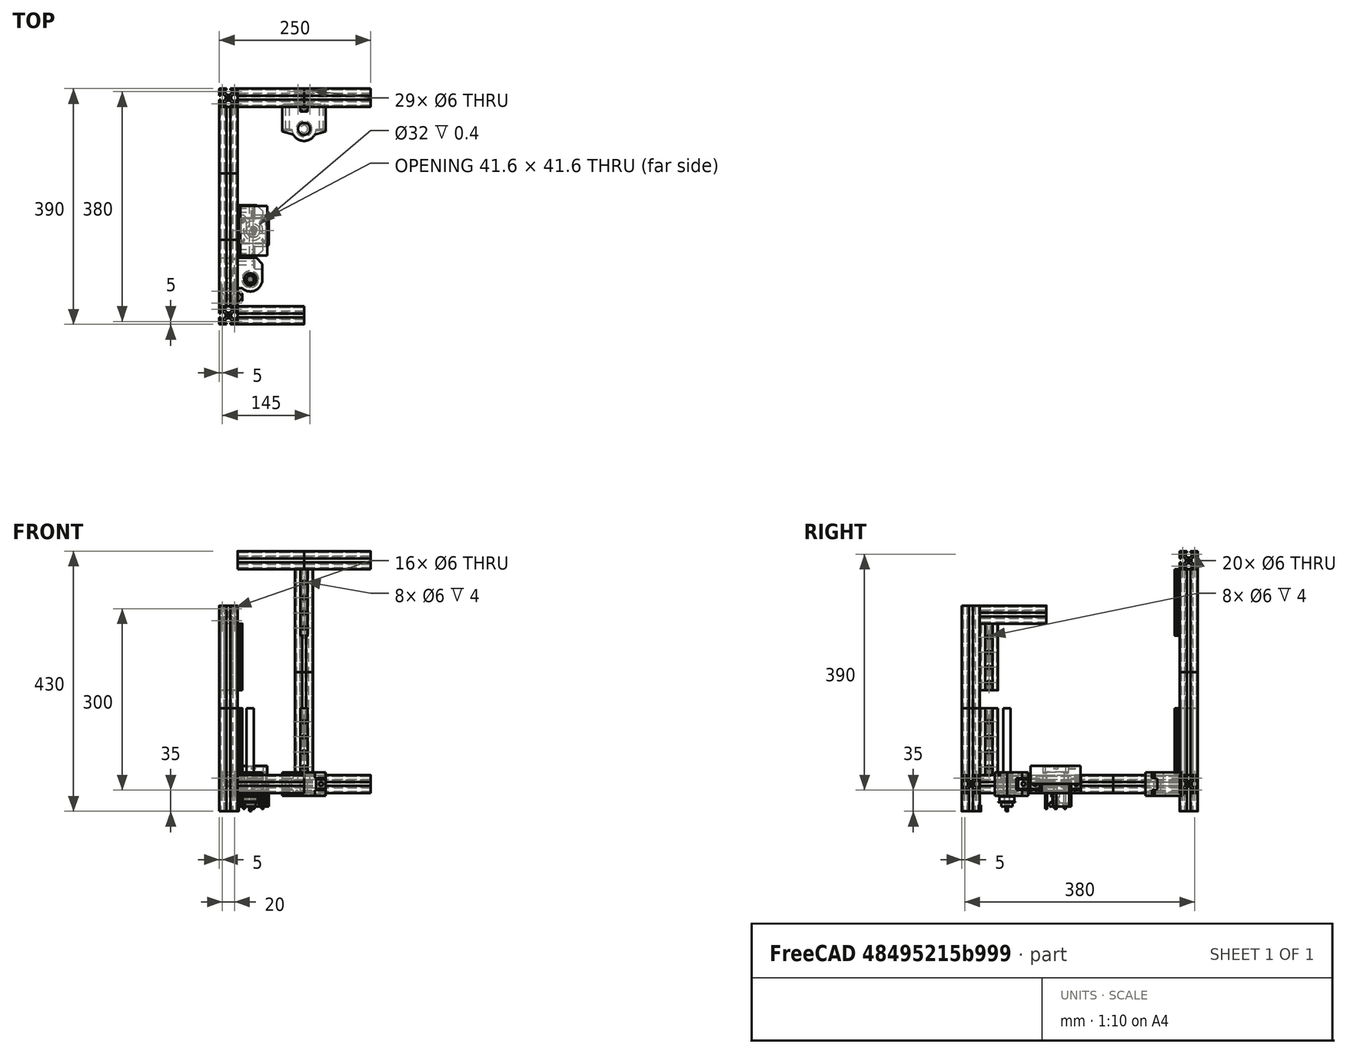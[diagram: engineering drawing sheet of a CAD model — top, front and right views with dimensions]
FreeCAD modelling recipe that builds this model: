
FCSTD DOCUMENT  (FreeCAD 0.18R16146 (Git))
Label: z-belt
License: All rights reserved
LicenseURL: http://en.wikipedia.org/wiki/All_rights_reserved
objects: Part::Cylinder×31, Part::Box×30, Part::Feature×29, Part::Chamfer×21, Part::MultiFuse×16, Part::Cut×15, App::DocumentObjectGroup×1, Part::Fillet×1
note: 143 computed .brp shape members not serialized (recipe doc carries the construction recipe); baked Part::Feature solids carry a one-line shape summary decoded from their .brp

FEATURE [Part::Feature] Fusion002  label="extrusion-3030-002"
  Placement = pos=(-7e-15,0,30) rot=(0,1,0;1.5708rad)
  shape: bbox 110 x 30 x 30 mm, 63 faces (baked)
FEATURE [Part::Feature] Fusion003  label="extrusion-3030-003"
  Placement = pos=(-30,-7e-15,30) rot=(0.57735,-0.57735,-0.57735;4.18879rad)
  shape: bbox 30 x 110 x 30 mm, 63 faces (baked)
FEATURE [Part::Feature] Fusion004  label="extrusion-3030-004"
  Placement = pos=(0,30,60) rot=(0,0,1;0rad)
  shape: bbox 30 x 30 x 110 mm, 63 faces (baked)
FEATURE [Part::Feature] Fusion006  label="extrusion-3030-001"
  shape: bbox 30 x 30 x 170 mm, 63 faces (baked)
FEATURE [Part::Feature] Common001  label="MGN12-rail"
  Placement = pos=(4,15,60) rot=(0.707107,0,0.707107;3.14159rad)
  shape: bbox 8 x 12 x 110 mm, 48 faces (baked)
FEATURE [Part::Feature] Chamfer001  label="SFU1204"
  Placement = pos=(21.15,44.62,10) rot=(0,0,1;0rad)
  shape: bbox 12 x 12 x 160 mm, 10 faces (baked)
FEATURE [Part::Feature] Cut001  label="pulley-40t"
  Placement = pos=(21.15,44.62,25) rot=(0,1,0;3.14159rad)
  shape: bbox 28 x 28 x 17 mm, 10 faces (baked)
FEATURE [Part::Cylinder] Cylinder  label="pos-4462-2115"
  Angle = 360
  AttacherType = Attacher::AttachEngine3D
  Height = 10
  Placement = pos=(21.15,44.52,0) rot=(0,0,1;0rad)
  Radius = 2
FEATURE [Part::Cylinder] Cylinder001  label="pos-3659"
  Angle = 360
  AttacherType = Attacher::AttachEngine3D
  Height = 10
  Radius = 2
FEATURE [Part::Box] Box  label="Cube"
  AttacherType = Attacher::AttachEngine3D
  Height = 4
  Length = 71.15
  Placement = pos=(-30,30,60) rot=(0,0,1;0rad)
  Width = 50
FEATURE [Part::Feature] Cut002001  label="collar"
  Placement = pos=(21.15,44.62,55) rot=(0,0,1;0rad)
  shape: bbox 18 x 18 x 8 mm, 7 faces (baked)
FEATURE [Part::Feature] Cut002002  label="thrust-bearing"
  Placement = pos=(21.15,44.62,49.5) rot=(0,0,1;0rad)
  shape: bbox 18 x 18 x 5.5 mm, 12 faces (baked)
FEATURE [Part::Feature] Chamfer002  label="6000zz"
  Placement = pos=(21.15,44.62,25.5) rot=(0,0,1;0rad)
  shape: bbox 26 x 26 x 8 mm, 8 faces (baked)
FEATURE [Part::Cylinder] Cylinder002  label="screw-cut"
  Angle = 360
  AttacherType = Attacher::AttachEngine3D
  Height = 15
  Placement = pos=(21.15,44.52,34.5) rot=(0,0,1;0rad)
  Radius = 6
FEATURE [Part::Cylinder] Cylinder003  label="top-bearing-cut"
  Angle = 360
  AttacherType = Attacher::AttachEngine3D
  Height = 15
  Placement = pos=(21.15,44.52,49.5) rot=(0,0,1;0rad)
  Radius = 10
FEATURE [Part::Cylinder] Cylinder004  label="btm-bearing-cut"
  Angle = 360
  AttacherType = Attacher::AttachEngine3D
  Height = 9
  Placement = pos=(21.15,44.52,25.5) rot=(0,0,1;0rad)
  Radius = 13.1
FEATURE [Part::Cylinder] Cylinder005  label="round-body"
  Angle = 360
  AttacherType = Attacher::AttachEngine3D
  Height = 38.5
  Placement = pos=(21.15,44.52,25.5) rot=(0,0,1;0rad)
  Radius = 20
FEATURE [Part::Box] Box003  label="Cube003"
  AttacherType = Attacher::AttachEngine3D
  Height = 6
  Length = 2
  Placement = pos=(-2,30,42) rot=(0,0,1;0rad)
  Width = 34.52
FEATURE [Part::Feature] Fusion007  label="extrusion-3030-005"
  Placement = pos=(-30,110,30) rot=(0.57735,-0.57735,-0.57735;4.18879rad)
  shape: bbox 30 x 110 x 30 mm, 63 faces (baked)
FEATURE [Part::Box] Box004  label="Cube004"
  AttacherType = Attacher::AttachEngine3D
  Height = 34.5
  Length = 41.15
  Placement = pos=(0,30.02,25.5) rot=(0,0,1;0rad)
  Width = 49.98
FEATURE [Part::Box] Box005  label="Cube005"
  AttacherType = Attacher::AttachEngine3D
  Height = 20
  Length = 41.15
  Placement = pos=(27,61.52,35) rot=(0,0,1;0rad)
  Width = 35.48
FEATURE [Part::MultiFuse] Fusion008
  Shapes = -> [Cylinder004,Cylinder003,Cylinder002]
FEATURE [Part::Cylinder] Cylinder006  label="Cylinder"
  Angle = 360
  AttacherType = Attacher::AttachEngine3D
  Height = 10
  Placement = pos=(-15,42.5,60) rot=(0,0,1;0rad)
  Radius = 3.2
FEATURE [Part::Cylinder] Cylinder007  label="Cylinder001"
  Angle = 360
  AttacherType = Attacher::AttachEngine3D
  Height = 33
  Placement = pos=(0,72,45) rot=(0,1,0;1.5708rad)
  Radius = 3.2
FEATURE [Part::Cylinder] Cylinder008  label="Cylinder002"
  Angle = 360
  AttacherType = Attacher::AttachEngine3D
  Height = 10
  Placement = pos=(-15,67.5,60) rot=(0,0,1;0rad)
  Radius = 3.2
FEATURE [Part::Feature] Cut002003006  label="Pulley-16T"
  Placement = pos=(26,125,15.3) rot=(0,0,1;3.14159rad)
  shape: bbox 13.9 x 13.9 x 15.5 mm, 10 faces (baked)
FEATURE [Part::Cylinder] Cylinder010  label="motor-center"
  Angle = 360
  AttacherType = Attacher::AttachEngine3D
  Height = 10
  Placement = pos=(26,125,4) rot=(0,0,1;0rad)
  Radius = 2
FEATURE [Part::Feature] Fusion001  label="nema17-39mm"
  Placement = pos=(26,125,10) rot=(0,0,1;0rad)
  shape: bbox 42 x 54 x 63 mm, 80 faces (baked)
FEATURE [Part::Feature] Chamfer014  label="MR115ZZ"
  Placement = pos=(26,125,10) rot=(0,0,1;0rad)
  shape: bbox 11 x 11 x 4 mm, 8 faces (baked)
FEATURE [Part::Box] Box006  label="Cube006"
  AttacherType = Attacher::AttachEngine3D
  Height = 30
  Length = 4.85
  Placement = pos=(0,83,30) rot=(0,0,1;0rad)
  Width = 84
FEATURE [Part::Box] Box008  label="Cube008"
  AttacherType = Attacher::AttachEngine3D
  Height = 30
  Length = 48
  Placement = pos=(0,99,30) rot=(0,0,1;0rad)
  Width = 4.85
FEATURE [Part::Box] Box009  label="Cube009"
  AttacherType = Attacher::AttachEngine3D
  Height = 30
  Length = 48
  Placement = pos=(0,146.15,30) rot=(0,0,1;0rad)
  Width = 4.85
FEATURE [Part::Box] Box010  label="Cube010"
  AttacherType = Attacher::AttachEngine3D
  Height = 15
  Length = 4.85
  Placement = pos=(47.15,99,30) rot=(0,0,1;0rad)
  Width = 52
FEATURE [Part::Cylinder] Cylinder011  label="center-slot"
  Angle = 360
  AttacherType = Attacher::AttachEngine3D
  Height = 23
  Placement = pos=(26,125,23) rot=(0,0,1;0rad)
  Radius = 11.05
FEATURE [Part::Box] Box011  label="Cube011"
  AttacherType = Attacher::AttachEngine3D
  Height = 4
  Length = 52
  Placement = pos=(0,99,30) rot=(0,0,1;0rad)
  Width = 52
FEATURE [Part::Cylinder] Cylinder012  label="motor-bolt-4"
  Angle = 360
  AttacherType = Attacher::AttachEngine3D
  Height = 47
  Placement = pos=(41.5,140.5,4) rot=(0,0,1;0rad)
  Radius = 1.6
FEATURE [Part::Cylinder] Cylinder013  label="motor-bolt-3"
  Angle = 360
  AttacherType = Attacher::AttachEngine3D
  Height = 47
  Placement = pos=(10.5,140.5,4) rot=(0,0,1;0rad)
  Radius = 1.6
FEATURE [Part::Cylinder] Cylinder014  label="motor-bolt-2"
  Angle = 360
  AttacherType = Attacher::AttachEngine3D
  Height = 47
  Placement = pos=(10.5,109.5,4) rot=(0,0,1;0rad)
  Radius = 1.6
FEATURE [Part::Cylinder] Cylinder015  label="motor-bolt-1"
  Angle = 360
  AttacherType = Attacher::AttachEngine3D
  Height = 47
  Placement = pos=(41.5,109.5,4) rot=(0,0,1;0rad)
  Radius = 1.6
FEATURE [Part::Cylinder] Cylinder016  label="motor-bolt-005"
  Angle = 360
  AttacherType = Attacher::AttachEngine3D
  Height = 47
  Placement = pos=(41.5,140.5,4) rot=(0,0,1;0rad)
  Radius = 1.6
FEATURE [Part::Cylinder] Cylinder017  label="motor-bolt-006"
  Angle = 360
  AttacherType = Attacher::AttachEngine3D
  Height = 47
  Placement = pos=(41.5,109.5,4) rot=(0,0,1;0rad)
  Radius = 1.6
FEATURE [Part::Cylinder] Cylinder018  label="motor-bolt-007"
  Angle = 360
  AttacherType = Attacher::AttachEngine3D
  Height = 47
  Placement = pos=(10.5,109.5,4) rot=(0,0,1;0rad)
  Radius = 1.6
FEATURE [Part::Cylinder] Cylinder019  label="motor-bolt-008"
  Angle = 360
  AttacherType = Attacher::AttachEngine3D
  Height = 47
  Placement = pos=(10.5,140.5,4) rot=(0,0,1;0rad)
  Radius = 1.6
FEATURE [Part::MultiFuse] Fusion011
  Shapes = -> [Cylinder015,Cylinder014,Cylinder013,Cylinder012]
FEATURE [Part::Cut] Cut002003007
  Base = -> Box011
  Tool = -> Fusion011
FEATURE [Part::Box] Box012  label="Cube012"
  AttacherType = Attacher::AttachEngine3D
  Height = 30
  Length = 44
  Placement = pos=(5,84,63) rot=(0,0,1;0rad)
  Width = 82
FEATURE [Part::Chamfer] Chamfer018
  Base = -> Box012
  Edges = 1 edges r=15: [Edge4]
  Placement = pos=(0,0,-18) rot=(0,0,1;0rad)
FEATURE [Part::Cylinder] Cylinder020  label="Cylinder004"
  Angle = 360
  AttacherType = Attacher::AttachEngine3D
  Height = 46
  Placement = pos=(0,91,45) rot=(0,1,0;1.5708rad)
  Radius = 3.2
FEATURE [Part::Cylinder] Cylinder021  label="Cylinder005"
  Angle = 360
  AttacherType = Attacher::AttachEngine3D
  Height = 46
  Placement = pos=(0,159,45) rot=(0,1,0;1.5708rad)
  Radius = 3.2
FEATURE [Part::Cut] Cut002003010
  Base = -> Cut002003007
  Tool = -> Cylinder011
FEATURE [Part::Box] Box013  label="Cube013"
  AttacherType = Attacher::AttachEngine3D
  Height = 22
  Length = 52
  Placement = pos=(0,121,8) rot=(0,0,1;0rad)
  Width = 30
FEATURE [Part::Cylinder] Cylinder024  label="shhaft-cut"
  Angle = 360
  AttacherType = Attacher::AttachEngine3D
  Height = 10
  Placement = pos=(26,125,7) rot=(0,0,1;0rad)
  Radius = 3
FEATURE [Part::Cylinder] Cylinder025  label="shaft-br-cut"
  Angle = 360
  AttacherType = Attacher::AttachEngine3D
  Height = 4
  Placement = pos=(26,125,10) rot=(0,0,1;0rad)
  Radius = 5.6
FEATURE [Part::Box] Box014  label="Cube014"
  AttacherType = Attacher::AttachEngine3D
  Height = 16
  Length = 32
  Placement = pos=(10,96,14) rot=(0,0,1;0rad)
  Width = 30
FEATURE [Part::Cylinder] Cylinder027  label="Cylinder008"
  Angle = 360
  AttacherType = Attacher::AttachEngine3D
  Height = 6
  Placement = pos=(26,125,8) rot=(0,0,1;0rad)
  Radius = 10
FEATURE [Part::MultiFuse] Fusion018
  Shapes = -> [Box013,Cylinder027]
FEATURE [Part::Chamfer] Chamfer020
  Base = -> Box014
  Edges = 2 edges r=5: [Edge3,Edge7]
FEATURE [Part::Chamfer] Chamfer021
  Base = -> Fusion018
  Edges = 2 edges r=5: [Edge1,Edge10]
FEATURE [Part::Chamfer] Chamfer023
  Base = -> Chamfer021
  Edges = 2 edges r=3: [Edge3,Edge13]
FEATURE [Part::Cylinder] Cylinder030  label="motor-bolt-011"
  Angle = 360
  AttacherType = Attacher::AttachEngine3D
  Height = 47
  Placement = pos=(10.5,140.5,4) rot=(0,0,1;0rad)
  Radius = 1.65
FEATURE [Part::Cylinder] Cylinder031  label="motor-bolt-012"
  Angle = 360
  AttacherType = Attacher::AttachEngine3D
  Height = 47
  Placement = pos=(41.5,140.5,4) rot=(0,0,1;0rad)
  Radius = 1.65
FEATURE [Part::MultiFuse] Fusion020
  Shapes = -> [Cylinder017,Cylinder018,Cylinder019,Cylinder016]
FEATURE [Part::Cylinder] Cylinder032  label="motor-bolt-013"
  Angle = 360
  AttacherType = Attacher::AttachEngine3D
  Height = 5
  Placement = pos=(41.5,140.5,4) rot=(0,0,1;0rad)
  Radius = 3.5
FEATURE [Part::Cylinder] Cylinder033  label="motor-bolt-014"
  Angle = 360
  AttacherType = Attacher::AttachEngine3D
  Height = 5
  Placement = pos=(10.5,140.5,4) rot=(0,0,1;0rad)
  Radius = 3.5
FEATURE [Part::MultiFuse] Fusion021
  Shapes = -> [Cylinder030,Cylinder031]
FEATURE [Part::MultiFuse] Fusion022
  Placement = pos=(0,0,3) rot=(0,0,1;0rad)
  Shapes = -> [Cylinder032,Cylinder033]
FEATURE [Part::Box] Box015  label="Cube015"
  AttacherType = Attacher::AttachEngine3D
  Height = 22
  Length = 34
  Placement = pos=(9,145,8) rot=(0,0,1;0rad)
  Width = 10
FEATURE [Part::Chamfer] Chamfer024
  Base = -> Box015
  Edges = 2 edges r=7: [Edge1,Edge5]
FEATURE [Part::Box] Box016  label="Cube016"
  AttacherType = Attacher::AttachEngine3D
  Height = 16
  Length = 22
  Placement = pos=(15,121,14) rot=(0,0,1;0rad)
  Width = 30
FEATURE [Part::Feature] Fusion023  label="extrusion-3030-006"
  Placement = pos=(-30,220,30) rot=(0.57735,-0.57735,-0.57735;4.18879rad)
  shape: bbox 30 x 110 x 30 mm, 63 faces (baked)
FEATURE [Part::Feature] Fusion024  label="extrusion-3030-007"
  Placement = pos=(0,360,0) rot=(0,0,1;0rad)
  shape: bbox 30 x 30 x 170 mm, 63 faces (baked)
FEATURE [Part::Feature] Fusion025  label="extrusion-3030-008"
  Placement = pos=(-7e-15,360,30) rot=(0,1,0;1.5708rad)
  shape: bbox 110 x 30 x 30 mm, 63 faces (baked)
FEATURE [Part::Feature] Fusion026  label="extrusion-3030-009"
  Placement = pos=(110,360,30) rot=(0,1,0;1.5708rad)
  shape: bbox 110 x 30 x 30 mm, 63 faces (baked)
FEATURE [Part::Feature] Fusion027  label="extrusion-3030-010"
  Placement = pos=(125,360,60) rot=(0,0,1;0rad)
  shape: bbox 30 x 30 x 170 mm, 63 faces (baked)
FEATURE [Part::Feature] Fusion008001  label="bearing-cut-slot"
  Placement = pos=(88.85,248.79,0) rot=(0,0,1;0rad)
  shape: bbox 26.2 x 26.2 x 39 mm, 7 faces (baked)
FEATURE [Part::Feature] Common002  label="MGN12-rail001"
  Placement = pos=(110,326,60) rot=(0.57735,-0.57735,0.57735;2.0944rad)
  shape: bbox 12 x 8 x 110 mm, 48 faces (baked)
FEATURE [Part::Box] Box017  label="Cube017"
  AttacherType = Attacher::AttachEngine3D
  Height = 38.5
  Length = 72
  Placement = pos=(74,284,25.5) rot=(0,0,1;0rad)
  Width = 46
FEATURE [Part::Box] Box018  label="Cube018"
  AttacherType = Attacher::AttachEngine3D
  Height = 4
  Length = 72
  Placement = pos=(74,330,60) rot=(0,0,1;0rad)
  Width = 4
FEATURE [Part::Box] Box019  label="Cube019"
  AttacherType = Attacher::AttachEngine3D
  Height = 4
  Length = 72
  Placement = pos=(74,330,25.5) rot=(0,0,1;0rad)
  Width = 5
FEATURE [Part::Box] Box020  label="Cube020"
  AttacherType = Attacher::AttachEngine3D
  Height = 20
  Length = 72
  Placement = pos=(74,284,35) rot=(0,0,1;0rad)
  Width = 9
FEATURE [Part::Box] Box021  label="Cube021"
  AttacherType = Attacher::AttachEngine3D
  Height = 6
  Length = 46
  Placement = pos=(87,330,42) rot=(0,0,1;0rad)
  Width = 2
FEATURE [Part::Cylinder] Cylinder035  label="Cylinder010"
  Angle = 360
  AttacherType = Attacher::AttachEngine3D
  Height = 46
  Placement = pos=(82,330,45) rot=(1,0,0;1.5708rad)
  Radius = 3.2
FEATURE [Part::Cylinder] Cylinder036  label="Cylinder011"
  Angle = 360
  AttacherType = Attacher::AttachEngine3D
  Height = 46
  Placement = pos=(138,330,45) rot=(1,0,0;1.5708rad)
  Radius = 3.2
FEATURE [Part::Box] Box022  label="Cube022"
  AttacherType = Attacher::AttachEngine3D
  Height = 4
  Length = 30.4
  Placement = pos=(94.8,329.8,60) rot=(0,0,1;0rad)
  Width = 2.2
FEATURE [Part::Box] Box023  label="Cube023"
  AttacherType = Attacher::AttachEngine3D
  Height = 4
  Length = 12.4
  Placement = pos=(103.8,321.8,60) rot=(0,0,1;0rad)
  Width = 10
FEATURE [Part::MultiFuse] Fusion008004
  Shapes = -> [Box023,Box022]
FEATURE [Part::Feature] Fusion008008  label="extrusion-3030-011"
  Placement = pos=(0,0,170) rot=(0,0,1;0rad)
  shape: bbox 30 x 30 x 170 mm, 63 faces (baked)
FEATURE [Part::Feature] Fusion008009  label="extrusion-3030-012"
  Placement = pos=(0,30,200) rot=(0,0,1;0rad)
  shape: bbox 30 x 30 x 110 mm, 63 faces (baked)
FEATURE [Part::Feature] Fusion008010  label="extrusion-3030-013"
  Placement = pos=(-30,-7e-15,310) rot=(0.57735,-0.57735,-0.57735;4.18879rad)
  shape: bbox 30 x 110 x 30 mm, 63 faces (baked)
FEATURE [Part::Feature] Common003  label="MGN12-rail002"
  Placement = pos=(4,15,200) rot=(0.707107,0,0.707107;3.14159rad)
  shape: bbox 8 x 12 x 110 mm, 48 faces (baked)
FEATURE [Part::Feature] Fusion008011  label="extrusion-3030-014"
  Placement = pos=(125,360,230) rot=(0,0,1;0rad)
  shape: bbox 30 x 30 x 170 mm, 63 faces (baked)
FEATURE [Part::Feature] Fusion008012  label="extrusion-3030-015"
  Placement = pos=(110,360,400) rot=(0,1,0;1.5708rad)
  shape: bbox 110 x 30 x 30 mm, 63 faces (baked)
FEATURE [Part::Feature] Fusion008013  label="extrusion-3030-016"
  Placement = pos=(-8.5e-14,360,400) rot=(0,1,0;1.5708rad)
  shape: bbox 110 x 30 x 30 mm, 63 faces (baked)
FEATURE [Part::Feature] Common004  label="MGN12-rail003"
  Placement = pos=(110,326,290) rot=(0.57735,-0.57735,0.57735;2.0944rad)
  shape: bbox 12 x 8 x 110 mm, 48 faces (baked)
FEATURE [App::DocumentObjectGroup] Group  label="Preference"
  Group = -> [Fusion002,Fusion003,Fusion004,Fusion006,Common001,Chamfer001,Cut001,Cylinder,Cylinder001,Cut002001,Cut002002,Chamfer002,Fusion007,Cut002003006,Cylinder010,Fusion001,Chamfer014,Fusion023,Fusion024,Fusion025,Fusion026,Fusion027,Common002,Fusion008008,Fusion008009,Fusion008010,Common003,Fusion008011,Fusion008012,Fusion008013,Common004]
FEATURE [Part::Box] Box024  label="Cube024"
  AttacherType = Attacher::AttachEngine3D
  Height = 4.5
  Length = 5
  Placement = pos=(-5,30.02,25.5) rot=(0,0,1;0rad)
  Width = 49.98
FEATURE [Part::Chamfer] Chamfer
  Base = -> Box
  Edges = 1 edges r=15: [Edge5]
FEATURE [Part::Chamfer] Chamfer033
  Base = -> Box004
  Edges = 1 edges r=15: [Edge5]
FEATURE [Part::MultiFuse] Fusion
  Shapes = -> [Box024,Chamfer033,Cylinder005,Chamfer,Box003]
FEATURE [Part::Cut] Cut
  Base = -> Fusion
  Tool = -> Box005
FEATURE [Part::Fillet] Fillet001
  Base = -> Cut
  Edges = 1 edges r=0.7: [Edge9]
FEATURE [Part::Chamfer] Chamfer034
  Base = -> Fillet001
  Edges = 3 edges r=10: [Edge45,Edge47,Edge71]
FEATURE [Part::Chamfer] Chamfer035
  Base = -> Chamfer034
  Edges = 1 edges r=1: [Edge26]
FEATURE [Part::Chamfer] Chamfer036
  Base = -> Chamfer035
  Edges = 2 edges r=3: [Edge69,Edge93]
FEATURE [Part::MultiFuse] Fusion008014
  Shapes = -> [Cylinder006,Cylinder008]
FEATURE [Part::Cut] Cut002003021002
  Base = -> Chamfer036
  Tool = -> Fusion008014
FEATURE [Part::Chamfer] Chamfer037
  Base = -> Cut002003021002
  Edges = 3 edges r=2: [Edge80,Edge85,Edge86]
FEATURE [Part::Cut] Cut002003021003
  Base = -> Chamfer037
  Tool = -> Cylinder007
FEATURE [Part::Cylinder] Cylinder034  label="Cylinder009"
  Angle = 360
  AttacherType = Attacher::AttachEngine3D
  Height = 38.5
  Placement = pos=(110,293.41,25.5) rot=(0,0,-1;1.5708rad)
  Radius = 20
FEATURE [Part::MultiFuse] Fusion008016
  Shapes = -> [Cylinder035,Cylinder036]
FEATURE [Part::MultiFuse] Fusion008017
  Shapes = -> [Box017,Box019,Box021,Box018]
FEATURE [Part::Cut] Cut002003021004
  Base = -> Fusion008017
  Tool = -> Box020
FEATURE [Part::Chamfer] Chamfer038
  Base = -> Cut002003021004
  Edges = 2 edges r=2: [Edge14,Edge17]
FEATURE [Part::Chamfer] Chamfer039
  Base = -> Chamfer038
  Edges = 2 edges: [Edge3 r1=5 r2=19,Edge10 r1=5 r2=19]
FEATURE [Part::Chamfer] Chamfer040
  Base = -> Chamfer039
  Edges = 1 edges: [Edge51 r1=5 r2=19]
FEATURE [Part::Chamfer] Chamfer041
  Base = -> Chamfer040
  Edges = 1 edges: [Edge22 r1=5 r2=19]
FEATURE [Part::MultiFuse] Fusion008018
  Shapes = -> [Chamfer041,Cylinder034]
FEATURE [Part::Cut] Cut002003021005
  Base = -> Fusion008018
  Tool = -> Fusion008016
FEATURE [Part::Cut] Cut002003021006
  Base = -> Cut002003021005
  Tool = -> Fusion008004
FEATURE [Part::MultiFuse] Fusion008019
  Shapes = -> [Fusion021,Fusion022]
FEATURE [Part::Cut] Cut002003021007
  Base = -> Chamfer023
  Tool = -> Chamfer020
FEATURE [Part::Cut] Cut002003021008
  Base = -> Cut002003021007
  Tool = -> Fusion008019
FEATURE [Part::Cut] Cut002003021009
  Base = -> Cut002003021008
  Tool = -> Chamfer024
FEATURE [Part::Cut] Cut002003021010
  Base = -> Cut002003021009
  Tool = -> Box016
FEATURE [Part::Cut] Cut002003021011
  Base = -> Cut002003021010
  Tool = -> Cylinder024
FEATURE [Part::Box] Box025  label="Cube025"
  AttacherType = Attacher::AttachEngine3D
  Height = 30
  Length = 27
  Placement = pos=(0,83,30) rot=(0,0,1;0rad)
  Width = 16
FEATURE [Part::Box] Box026  label="Cube026"
  AttacherType = Attacher::AttachEngine3D
  Height = 30
  Length = 27
  Placement = pos=(0,151,30) rot=(0,0,1;0rad)
  Width = 16
FEATURE [Part::Box] Box027  label="Cube027"
  AttacherType = Attacher::AttachEngine3D
  Height = 5
  Length = 15
  Placement = pos=(27,83,30) rot=(0,0,1;0rad)
  Width = 16
FEATURE [Part::Box] Box028  label="Cube028"
  AttacherType = Attacher::AttachEngine3D
  Height = 5
  Length = 15
  Placement = pos=(27,83,55) rot=(0,0,1;0rad)
  Width = 16
FEATURE [Part::Box] Box029  label="Cube029"
  AttacherType = Attacher::AttachEngine3D
  Height = 5
  Length = 15
  Placement = pos=(27,151,30) rot=(0,0,1;0rad)
  Width = 16
FEATURE [Part::Box] Box030  label="Cube030"
  AttacherType = Attacher::AttachEngine3D
  Height = 5
  Length = 15
  Placement = pos=(27,151,55) rot=(0,0,1;0rad)
  Width = 16
FEATURE [Part::MultiFuse] Fusion008020
  Shapes = -> [Box028,Box025,Box027,Box030,Box026,Box029,Box009,Box008,Box006]
FEATURE [Part::Chamfer] Chamfer042
  Base = -> Fusion008020
  Edges = 4 edges r=2: [Edge17,Edge34,Edge110,Edge111]
FEATURE [Part::Box] Box031  label="Cube031"
  AttacherType = Attacher::AttachEngine3D
  Height = 6
  Length = 2
  Placement = pos=(-2,99,42) rot=(0,0,1;0rad)
  Width = 52
FEATURE [Part::Box] Box032  label="Cube032"
  AttacherType = Attacher::AttachEngine3D
  Height = 15
  Length = 12
  Placement = pos=(42,99,45) rot=(0,0,1;0rad)
  Width = 52
FEATURE [Part::MultiFuse] Fusion008021
  Shapes = -> [Box010,Cut002003010,Chamfer042,Box031]
FEATURE [Part::MultiFuse] Fusion008022
  Shapes = -> [Cylinder021,Cylinder020]
FEATURE [Part::Cut] Cut002003021012
  Base = -> Fusion008021
  Tool = -> Fusion008022
FEATURE [Part::Chamfer] Chamfer043
  Base = -> Box032
  Edges = 1 edges r=5: [Edge4]
FEATURE [Part::Cut] Cut002003021013
  Base = -> Cut002003021012
  Tool = -> Chamfer043
FEATURE [Part::Chamfer] Chamfer044
  Base = -> Cut002003021013
  Edges = 4 edges r=10: [Edge43,Edge133,Edge200,Edge230]
FEATURE [Part::Chamfer] Chamfer045
  Base = -> Chamfer044
  Edges = 4 edges r=3: [Edge67,Edge100,Edge110,Edge150]
FEATURE [Part::Chamfer] Chamfer046
  Base = -> Cut002003021006
  Edges = 2 edges r=2: [Edge100,Edge126]
FEATURE [Part::Chamfer] Chamfer047
  Base = -> Chamfer046
  Edges = 2 edges r=3: [Edge70,Edge125]
